# Revit family: НЕВАТОМ_Нaгреватель NWP, Версия 2
name_source: partatom
category: Обобщенные модели
revit_build: Autodesk Revit 2017 (Build: 20170118_1100(x64)
units: mm (PartAtom-declared; Revit-internal decimal feet)

## family parameters
Всегда вертикально = Да
Может служить основой для арматурных стержней = Нет
На основе рабочей плоскости = Нет
Общий = Нет
При загрузке вырезать с полостями = Нет
Размер круглого соединителя = Использовать диаметр
Тип детали = Нормальный
Точка расчета площади = Нет

## types (1)
- НЕВАТОМ_Нaгреватель NWP, Версия 2
    100 = 100 мм
    20 = 20 мм
    ADSK_Единица измерения = шт.
    ADSK_Завод-изготовитель = НЕВАТОМ
    ADSK_Количество = 1
    ADSK_Материал наименование = Оцинкованная сталь
    ADSK_Наименование = Нагреватель водяной прямоугольный
    ADSK_Примечание = Подбор осуществляется  по "ADSK_Номинальная мощность" и "ADSK_Потеря давления воздуха"
    a = 150 мм
    Материал = Оцинкованная сталь
    НЕВАТОМ_URL = https://t.me
    НЕВАТОМ_Температура воды на входе в нагреватель = 90 °C
    НЕВАТОМ_Температура воды на выходе из нагревателя = 70 °C
    ТП = nwp
